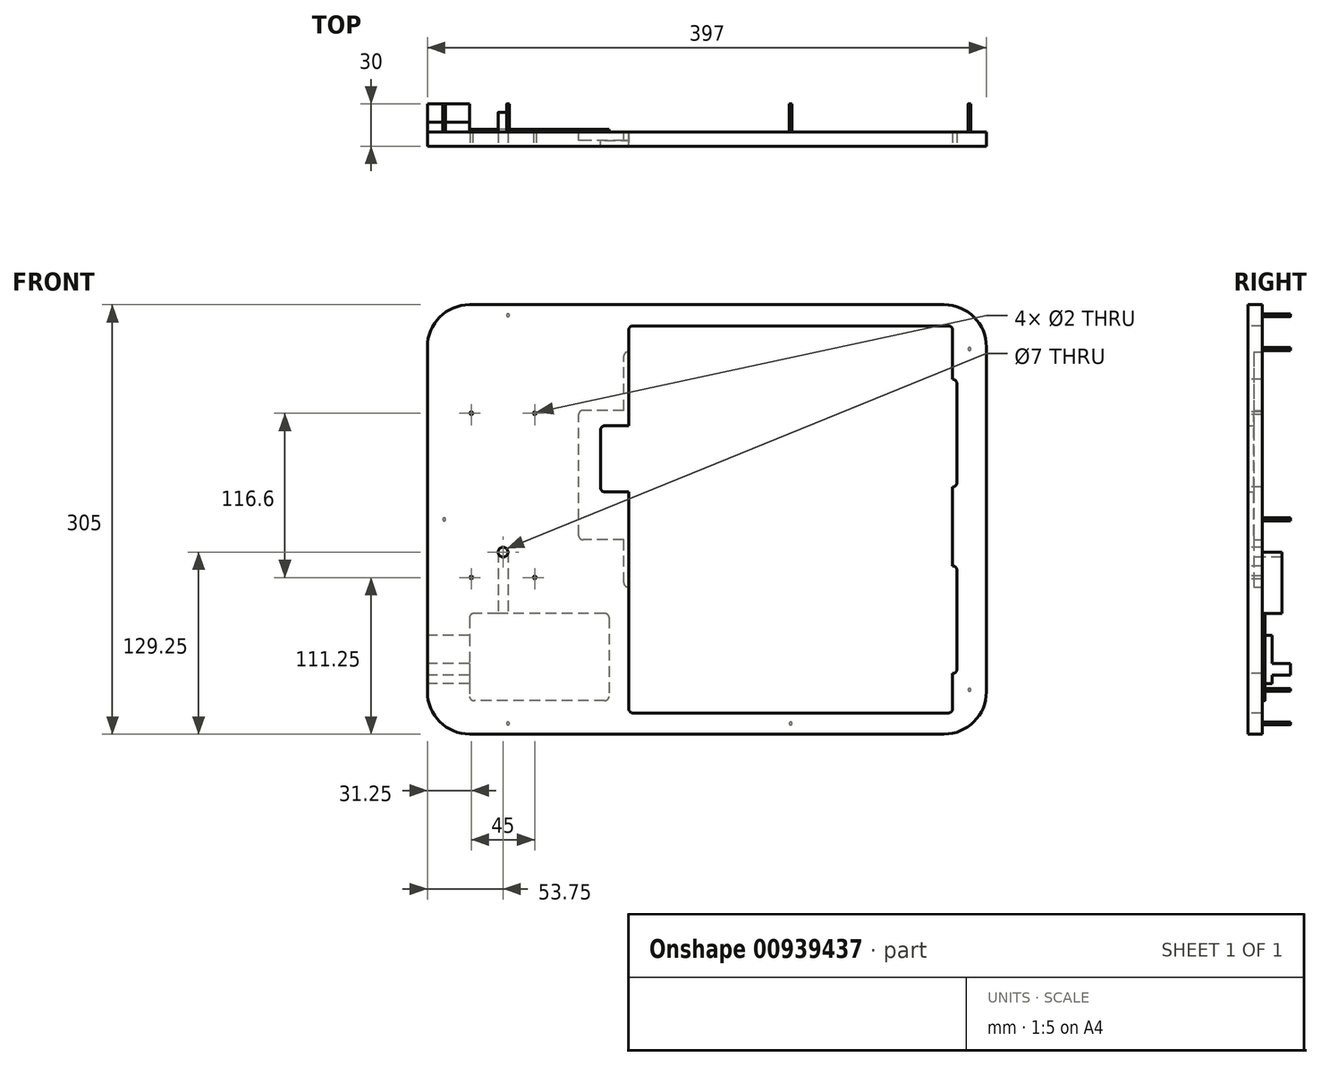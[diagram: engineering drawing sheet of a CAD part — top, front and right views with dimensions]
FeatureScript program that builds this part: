
annotation { "Feature Type Name" : "Feature", "Feature Type Description" : "" }
export const myFeature = defineFeature(function(context is Context, id is Id, definition is map)
    precondition{}
    {
        {
            var Q0;
            Q0=qCreatedBy(makeId("Front.planeOp"),FACE);
            var sketch = newSketch(context, id + "F0", { "sketchPlane" : qUnion([Q0])});
            skLineSegment(sketch, "E0.bottom", {"start": v(-198.5, 157.5) * mm, "end": v(198.5, 157.5) * mm});
            skLineSegment(sketch, "E0.top", {"start": v(-198.5, -147.5) * mm, "end": v(198.5, -147.5) * mm});
            skLineSegment(sketch, "E0.left", {"start": v(-198.5, 157.5) * mm, "end": v(-198.5, -147.5) * mm});
            skLineSegment(sketch, "E0.right", {"start": v(198.5, 157.5) * mm, "end": v(198.5, -147.5) * mm});
            skSolve(sketch);
        }
        {
            var Q0;
            Q0=makeQuery(id+"F0.imprint","IMPRINT",FACE,{"disambiguationData":[TD([[makeQuery(id+"F0.imprint","IMPRINT",EDGE,{"derivedFrom":sQuery(id+"F0.wireOp",EDGE,"E0.bottom")}),-1.0]])]});
            extrude(context, id + "F1", {"entities" : qUnion([Q0]), "depth" : 30 * mm, "offsetDistance" : 25 * mm});
        }
        {
            var Q0;
            Q0=makeQuery(id+"F1.opExtrude","CAP_FACE",FACE,{"disambiguationData":[OSD([sQuery(id+"F0.wireOp",EDGE,"E0.bottom"),sQuery(id+"F0.wireOp",EDGE,"E0.top"),sQuery(id+"F0.wireOp",EDGE,"E0.left"),sQuery(id+"F0.wireOp",EDGE,"E0.right")])],"isStart":false});
            var sketch = newSketch(context, id + "F2", { "sketchPlane" : qUnion([Q0])});
            skLineSegment(sketch, "E1.bottom", {"start": v(-55.5, 142.5) * mm, "end": v(174.5, 142.5) * mm});
            skLineSegment(sketch, "E1.top", {"start": v(-55.5, -132.5) * mm, "end": v(174.5, -132.5) * mm});
            skLineSegment(sketch, "E1.left", {"start": v(-55.5, 142.5) * mm, "end": v(-55.5, -132.5) * mm});
            skLineSegment(sketch, "E1.right", {"start": v(174.5, 142.5) * mm, "end": v(174.5, -132.5) * mm});
            skSolve(sketch);
        }
        {
            var Q0;
            Q0 = qSketchRegion(id + "F2", true);
            extrude(context, id + "F3", {"entities" : qUnion([Q0]), "operationType" : NewBodyOperationType.REMOVE, "endBound" : BoundingType.UP_TO_NEXT, "oppositeDirection" : true, "depth" : 25 * mm, "offsetDistance" : 25 * mm});
        }
        {
            var Q0;
            Q0=makeQuery(id+"F3.boolean.opBoolean","COPY",EDGE,{"derivedFrom":makeQuery(id+"F3.opExtrude","SWEPT_EDGE",EDGE,{"disambiguationData":[OSD([sQuery(id+"F2.wireOp",EDGE,"E1.bottom"),sQuery(id+"F2.wireOp",EDGE,"E1.left")])]})});
            var Q1;
            Q1=makeQuery(id+"F3.boolean.opBoolean","COPY",EDGE,{"derivedFrom":makeQuery(id+"F3.opExtrude","SWEPT_EDGE",EDGE,{"disambiguationData":[OSD([sQuery(id+"F2.wireOp",EDGE,"E1.bottom"),sQuery(id+"F2.wireOp",EDGE,"E1.right")])]})});
            var Q2;
            Q2=makeQuery(id+"F3.boolean.opBoolean","COPY",EDGE,{"derivedFrom":makeQuery(id+"F3.opExtrude","SWEPT_EDGE",EDGE,{"disambiguationData":[OSD([sQuery(id+"F2.wireOp",EDGE,"E1.top"),sQuery(id+"F2.wireOp",EDGE,"E1.right")])]})});
            var Q3;
            Q3=makeQuery(id+"F3.boolean.opBoolean","COPY",EDGE,{"derivedFrom":makeQuery(id+"F3.opExtrude","SWEPT_EDGE",EDGE,{"disambiguationData":[OSD([sQuery(id+"F2.wireOp",EDGE,"E1.top"),sQuery(id+"F2.wireOp",EDGE,"E1.left")])]})});
            fillet(context, id + "F4", {"entities" : qUnion([Q0, Q1, Q2, Q3]), "radius" : 3 * mm, "tangentPropagation" : true, "allowEdgeOverflow" : false});
        }
        {
            var Q0;
            Q0=makeQuery(id+"F1.opExtrude","SWEPT_EDGE",EDGE,{"disambiguationData":[OSD([sQuery(id+"F0.wireOp",EDGE,"E0.top"),sQuery(id+"F0.wireOp",EDGE,"E0.left")])]});
            var Q1;
            Q1=makeQuery(id+"F1.opExtrude","SWEPT_EDGE",EDGE,{"disambiguationData":[OSD([sQuery(id+"F0.wireOp",EDGE,"E0.bottom"),sQuery(id+"F0.wireOp",EDGE,"E0.left")])]});
            var Q2;
            Q2=makeQuery(id+"F1.opExtrude","SWEPT_EDGE",EDGE,{"disambiguationData":[OSD([sQuery(id+"F0.wireOp",EDGE,"E0.bottom"),sQuery(id+"F0.wireOp",EDGE,"E0.right")])]});
            var Q3;
            Q3=makeQuery(id+"F1.opExtrude","SWEPT_EDGE",EDGE,{"disambiguationData":[OSD([sQuery(id+"F0.wireOp",EDGE,"E0.top"),sQuery(id+"F0.wireOp",EDGE,"E0.right")])]});
            fillet(context, id + "F5", {"entities" : qUnion([Q0, Q1, Q2, Q3]), "radius" : 30 * mm, "tangentPropagation" : true, "allowEdgeOverflow" : false});
        }
        {
            var Q0;
            Q0=makeQuery(id+"F3.boolean.opBoolean","COPY",FACE,{"derivedFrom":makeQuery(id+"F3.opExtrude","SWEPT_FACE",FACE,{"disambiguationData":[OSD([sQuery(id+"F2.wireOp",EDGE,"E1.left")])]})});
            var sketch = newSketch(context, id + "F6", { "sketchPlane" : qUnion([Q0])});
            skLineSegment(sketch, "E2.bottom", {"start": v(-26, 124) * mm, "end": v(0, 124) * mm});
            skLineSegment(sketch, "E2.top", {"start": v(-26, -43) * mm, "end": v(0, -43) * mm});
            skLineSegment(sketch, "E2.left", {"start": v(-26, 124) * mm, "end": v(-26, -43) * mm});
            skLineSegment(sketch, "E2.right", {"start": v(0, 124) * mm, "end": v(0, -43) * mm});
            skSolve(sketch);
        }
        {
            var Q0;
            Q0=makeQuery(id+"F6.imprint","IMPRINT",FACE,{"disambiguationData":[TD([[makeQuery(id+"F6.imprint","IMPRINT",EDGE,{"derivedFrom":sQuery(id+"F6.wireOp",EDGE,"E2.bottom")}),-1.0]])]});
            extrude(context, id + "F7", {"entities" : qUnion([Q0]), "operationType" : NewBodyOperationType.REMOVE, "oppositeDirection" : true, "depth" : 3.5 * mm, "offsetDistance" : 25 * mm});
        }
        {
            var Q0;
            Q0=makeQuery(id+"F7.boolean.opBoolean","COPY",EDGE,{"derivedFrom":makeQuery(id+"F7.opExtrude","CAP_EDGE",EDGE,{"disambiguationData":[OSD([sQuery(id+"F6.wireOp",EDGE,"E2.top")])],"isStart":false})});
            var Q1;
            Q1=makeQuery(id+"F7.boolean.opBoolean","COPY",EDGE,{"derivedFrom":makeQuery(id+"F7.opExtrude","CAP_EDGE",EDGE,{"disambiguationData":[OSD([sQuery(id+"F6.wireOp",EDGE,"E2.bottom")])],"isStart":false})});
            fillet(context, id + "F8", {"entities" : qUnion([Q0, Q1]), "radius" : 3 * mm, "tangentPropagation" : true, "allowEdgeOverflow" : false});
        }
        {
            var Q0;
            Q0=makeQuery(id+"F7.boolean.opBoolean","COPY",FACE,{"derivedFrom":makeQuery(id+"F7.opExtrude","CAP_FACE",FACE,{"disambiguationData":[OSD([sQuery(id+"F6.wireOp",EDGE,"E2.bottom"),sQuery(id+"F6.wireOp",EDGE,"E2.top"),sQuery(id+"F6.wireOp",EDGE,"E2.left"),sQuery(id+"F6.wireOp",EDGE,"E2.right")])],"isStart":false})});
            var sketch = newSketch(context, id + "F9", { "sketchPlane" : qUnion([Q0])});
            skLineSegment(sketch, "E3.bottom", {"start": v(-23.6, 82.5) * mm, "end": v(0, 82.5) * mm});
            skLineSegment(sketch, "E3.top", {"start": v(-23.6, -9.5) * mm, "end": v(0, -9.5) * mm});
            skLineSegment(sketch, "E3.left", {"start": v(-23.6, 82.5) * mm, "end": v(-23.6, -9.5) * mm});
            skLineSegment(sketch, "E3.right", {"start": v(0, 82.5) * mm, "end": v(0, -9.5) * mm});
            skSolve(sketch);
        }
        {
            var Q0;
            Q0=makeQuery(id+"F1.opExtrude","CAP_FACE",FACE,{"disambiguationData":[OSD([sQuery(id+"F0.wireOp",EDGE,"E0.bottom"),sQuery(id+"F0.wireOp",EDGE,"E0.top"),sQuery(id+"F0.wireOp",EDGE,"E0.left"),sQuery(id+"F0.wireOp",EDGE,"E0.right")])],"isStart":true});
            var sketch = newSketch(context, id + "F10", { "sketchPlane" : qUnion([Q0])});
            skLineSegment(sketch, "E4.bottom", {"start": v(59, -9.5) * mm, "end": v(91, -9.5) * mm});
            skLineSegment(sketch, "E4.top", {"start": v(59, 82.5) * mm, "end": v(91, 82.5) * mm});
            skLineSegment(sketch, "E4.left", {"start": v(59, -9.5) * mm, "end": v(59, 82.5) * mm});
            skLineSegment(sketch, "E4.right", {"start": v(91, -9.5) * mm, "end": v(91, 82.5) * mm});
            skSolve(sketch);
        }
        {
            var Q0;
            Q0 = qSketchRegion(id + "F10", true);
            extrude(context, id + "F11", {"entities" : qUnion([Q0]), "operationType" : NewBodyOperationType.REMOVE, "oppositeDirection" : true, "depth" : 26 * mm, "offsetDistance" : 25 * mm});
        }
        {
            var Q0;
            Q0=makeQuery(id+"F11.boolean.opBoolean","COPY",EDGE,{"derivedFrom":makeQuery(id+"F11.opExtrude","SWEPT_EDGE",EDGE,{"disambiguationData":[OSD([sQuery(id+"F10.wireOp",EDGE,"E4.bottom"),sQuery(id+"F10.wireOp",EDGE,"E4.right")])]})});
            var Q1;
            Q1=makeQuery(id+"F11.boolean.opBoolean","COPY",EDGE,{"derivedFrom":makeQuery(id+"F11.opExtrude","SWEPT_EDGE",EDGE,{"disambiguationData":[OSD([sQuery(id+"F10.wireOp",EDGE,"E4.top"),sQuery(id+"F10.wireOp",EDGE,"E4.right")])]})});
            fillet(context, id + "F12", {"entities" : qUnion([Q0, Q1]), "radius" : 3 * mm, "tangentPropagation" : true, "allowEdgeOverflow" : false});
        }
        {
            var Q0;
            Q0=makeQuery(id+"F3.boolean.opBoolean","COPY",FACE,{"derivedFrom":makeQuery(id+"F3.opExtrude","SWEPT_FACE",FACE,{"disambiguationData":[OSD([sQuery(id+"F2.wireOp",EDGE,"E1.left")])]})});
            var sketch = newSketch(context, id + "F13", { "sketchPlane" : qUnion([Q0])});
            skLineSegment(sketch, "E5.bottom", {"start": v(-30, 71.5) * mm, "end": v(-26, 71.5) * mm});
            skLineSegment(sketch, "E5.top", {"start": v(-30, 24.5) * mm, "end": v(-26, 24.5) * mm});
            skLineSegment(sketch, "E5.left", {"start": v(-30, 71.5) * mm, "end": v(-30, 24.5) * mm});
            skLineSegment(sketch, "E5.right", {"start": v(-26, 71.5) * mm, "end": v(-26, 24.5) * mm});
            skSolve(sketch);
        }
        {
            var Q0;
            Q0 = qSketchRegion(id + "F13", true);
            extrude(context, id + "F14", {"entities" : qUnion([Q0]), "operationType" : NewBodyOperationType.REMOVE, "oppositeDirection" : true, "depth" : 20 * mm, "offsetDistance" : 25 * mm});
        }
        {
            var Q0;
            Q0=makeQuery(id+"F14.boolean.opBoolean","COPY",EDGE,{"derivedFrom":makeQuery(id+"F14.opExtrude","CAP_EDGE",EDGE,{"disambiguationData":[OSD([sQuery(id+"F13.wireOp",EDGE,"E5.top")])],"isStart":false})});
            var Q1;
            Q1=makeQuery(id+"F14.boolean.opBoolean","COPY",EDGE,{"derivedFrom":makeQuery(id+"F14.opExtrude","CAP_EDGE",EDGE,{"disambiguationData":[OSD([sQuery(id+"F13.wireOp",EDGE,"E5.bottom")])],"isStart":false})});
            fillet(context, id + "F15", {"entities" : qUnion([Q0, Q1]), "radius" : 3 * mm, "tangentPropagation" : true, "allowEdgeOverflow" : false});
        }
        {
            var Q0;
            Q0=makeQuery(id+"F3.boolean.opBoolean","COPY",FACE,{"derivedFrom":makeQuery(id+"F3.opExtrude","SWEPT_FACE",FACE,{"disambiguationData":[OSD([sQuery(id+"F2.wireOp",EDGE,"E1.right")])]})});
            var sketch = newSketch(context, id + "F16", { "sketchPlane" : qUnion([Q0])});
            skLineSegment(sketch, "E6.bottom", {"start": v(0, -28) * mm, "end": v(30, -28) * mm});
            skLineSegment(sketch, "E6.top", {"start": v(0, -104.5) * mm, "end": v(30, -104.5) * mm});
            skLineSegment(sketch, "E6.left", {"start": v(0, -28) * mm, "end": v(0, -104.5) * mm});
            skLineSegment(sketch, "E6.right", {"start": v(30, -28) * mm, "end": v(30, -104.5) * mm});
            skLineSegment(sketch, "E7.bottom", {"start": v(0, 104.5) * mm, "end": v(30, 104.5) * mm});
            skLineSegment(sketch, "E7.top", {"start": v(0, 28) * mm, "end": v(30, 28) * mm});
            skLineSegment(sketch, "E7.left", {"start": v(0, 104.5) * mm, "end": v(0, 28) * mm});
            skLineSegment(sketch, "E7.right", {"start": v(30, 104.5) * mm, "end": v(30, 28) * mm});
            skSolve(sketch);
        }
        {
            var Q0;
            Q0 = qSketchRegion(id + "F16", true);
            extrude(context, id + "F17", {"entities" : qUnion([Q0]), "operationType" : NewBodyOperationType.REMOVE, "oppositeDirection" : true, "depth" : 3 * mm, "offsetDistance" : 25 * mm});
        }
        {
            var Q0;
            Q0=makeQuery(id+"F17.boolean.opBoolean","COPY",EDGE,{"derivedFrom":makeQuery(id+"F17.opExtrude","CAP_EDGE",EDGE,{"disambiguationData":[OSD([sQuery(id+"F16.wireOp",EDGE,"E6.top")])],"isStart":false})});
            var Q1;
            Q1=makeQuery(id+"F17.boolean.opBoolean","COPY",EDGE,{"derivedFrom":makeQuery(id+"F17.opExtrude","CAP_EDGE",EDGE,{"disambiguationData":[OSD([sQuery(id+"F16.wireOp",EDGE,"E7.top")])],"isStart":false})});
            var Q2;
            Q2=makeQuery(id+"F17.boolean.opBoolean","COPY",EDGE,{"derivedFrom":makeQuery(id+"F17.opExtrude","CAP_EDGE",EDGE,{"disambiguationData":[OSD([sQuery(id+"F16.wireOp",EDGE,"E7.bottom")])],"isStart":false})});
            var Q3;
            Q3=makeQuery(id+"F17.boolean.opBoolean","COPY",EDGE,{"derivedFrom":makeQuery(id+"F17.opExtrude","CAP_EDGE",EDGE,{"disambiguationData":[OSD([sQuery(id+"F16.wireOp",EDGE,"E6.bottom")])],"isStart":false})});
            fillet(context, id + "F18", {"entities" : qUnion([Q0, Q1, Q2, Q3]), "radius" : 3 * mm, "tangentPropagation" : true, "allowEdgeOverflow" : false});
        }
        {
            var Q0;
            Q0=makeQuery(id+"F1.opExtrude","CAP_FACE",FACE,{"disambiguationData":[OSD([sQuery(id+"F0.wireOp",EDGE,"E0.bottom"),sQuery(id+"F0.wireOp",EDGE,"E0.top"),sQuery(id+"F0.wireOp",EDGE,"E0.left"),sQuery(id+"F0.wireOp",EDGE,"E0.right")])],"isStart":false});
            var sketch = newSketch(context, id + "F19", { "sketchPlane" : qUnion([Q0])});
            skCircle(sketch, "E8", {"center": v(-144.75, -18.25) * mm, "radius": 3.5 * mm});
            skSolve(sketch);
        }
        {
            var Q0;
            Q0 = qSketchRegion(id + "F19", true);
            extrude(context, id + "F20", {"entities" : qUnion([Q0]), "operationType" : NewBodyOperationType.REMOVE, "oppositeDirection" : true, "depth" : 30 * mm, "offsetDistance" : 25 * mm});
        }
        {
            var Q0;
            Q0=makeQuery(id+"F1.opExtrude","CAP_FACE",FACE,{"disambiguationData":[OSD([sQuery(id+"F0.wireOp",EDGE,"E0.bottom"),sQuery(id+"F0.wireOp",EDGE,"E0.top"),sQuery(id+"F0.wireOp",EDGE,"E0.left"),sQuery(id+"F0.wireOp",EDGE,"E0.right")])],"isStart":true});
            var sketch = newSketch(context, id + "F21", { "sketchPlane" : qUnion([Q0])});
            skLineSegment(sketch, "E9.bottom", {"start": v(69.5, -61.75) * mm, "end": v(168.5, -61.75) * mm});
            skLineSegment(sketch, "E9.top", {"start": v(69.5, -123.75) * mm, "end": v(168.5, -123.75) * mm});
            skLineSegment(sketch, "E9.left", {"start": v(69.5, -61.75) * mm, "end": v(69.5, -123.75) * mm});
            skLineSegment(sketch, "E9.right", {"start": v(168.5, -61.75) * mm, "end": v(168.5, -123.75) * mm});
            skSolve(sketch);
        }
        {
            var Q0;
            Q0 = qSketchRegion(id + "F21", true);
            var Q1;
            Q1 = qSketchRegion(id + "F24", true);
            extrude(context, id + "F22", {"entities" : qUnion([Q0, Q1]), "operationType" : NewBodyOperationType.REMOVE, "oppositeDirection" : true, "depth" : 18 * mm, "offsetDistance" : 25 * mm});
        }
        {
            var Q0;
            Q0=makeQuery(id+"F22.boolean.opBoolean","COPY",EDGE,{"derivedFrom":makeQuery(id+"F22.opExtrude","SWEPT_EDGE",EDGE,{"disambiguationData":[OSD([sQuery(id+"F21.wireOp",EDGE,"E9.top"),sQuery(id+"F21.wireOp",EDGE,"E9.right")])]})});
            var Q1;
            Q1=makeQuery(id+"F22.boolean.opBoolean","COPY",EDGE,{"derivedFrom":makeQuery(id+"F22.opExtrude","SWEPT_EDGE",EDGE,{"disambiguationData":[OSD([sQuery(id+"F21.wireOp",EDGE,"E9.top"),sQuery(id+"F21.wireOp",EDGE,"E9.left")])]})});
            var Q2;
            Q2=makeQuery(id+"F22.boolean.opBoolean","COPY",EDGE,{"derivedFrom":makeQuery(id+"F22.opExtrude","SWEPT_EDGE",EDGE,{"disambiguationData":[OSD([sQuery(id+"F21.wireOp",EDGE,"E9.bottom"),sQuery(id+"F21.wireOp",EDGE,"E9.left")])]})});
            var Q3;
            Q3=makeQuery(id+"F22.boolean.opBoolean","COPY",EDGE,{"derivedFrom":makeQuery(id+"F22.opExtrude","SWEPT_EDGE",EDGE,{"disambiguationData":[OSD([sQuery(id+"F21.wireOp",EDGE,"E9.bottom"),sQuery(id+"F21.wireOp",EDGE,"E9.right")])]})});
            fillet(context, id + "F23", {"entities" : qUnion([Q0, Q1, Q2, Q3]), "radius" : 3 * mm, "tangentPropagation" : true, "allowEdgeOverflow" : false});
        }
        {
            var Q0;
            Q0=makeQuery(id+"F1.opExtrude","CAP_FACE",FACE,{"disambiguationData":[OSD([sQuery(id+"F0.wireOp",EDGE,"E0.bottom"),sQuery(id+"F0.wireOp",EDGE,"E0.top"),sQuery(id+"F0.wireOp",EDGE,"E0.left"),sQuery(id+"F0.wireOp",EDGE,"E0.right")])],"isStart":true});
            var sketch = newSketch(context, id + "F24", { "sketchPlane" : qUnion([Q0])});
            skLineSegment(sketch, "E10", {"start": v(141.25, -18.25) * mm, "end": v(141.25, -61.75) * mm});
            skLineSegment(sketch, "E11", {"start": v(148.25, -18.25) * mm, "end": v(148.25, -61.75) * mm});
            skSolve(sketch);
        }
        {
            var Q0;
            {var subQ0=sQuery(id+"F24.wireOp",EDGE,"E10");Q0=makeQuery(id+"F24.imprint","IMPRINT",FACE,{"disambiguationData":[TD([[makeQuery(id+"F24.imprint","IMPRINT",EDGE,{"derivedFrom":subQ0}),1.0]])]});}
            extrude(context, id + "F25", {"entities" : qUnion([Q0]), "operationType" : NewBodyOperationType.REMOVE, "oppositeDirection" : true, "depth" : 6 * mm, "offsetDistance" : 25 * mm});
        }
        {
            var Q0;
            Q0=makeQuery(id+"F1.opExtrude","SWEPT_FACE",FACE,{"disambiguationData":[OSD([sQuery(id+"F0.wireOp",EDGE,"E0.left")])]});
            var sketch = newSketch(context, id + "F26", { "sketchPlane" : qUnion([Q0])});
            skLineSegment(sketch, "E12.bottom", {"start": v(0, -77.5) * mm, "end": v(13, -77.5) * mm});
            skLineSegment(sketch, "E12.top", {"start": v(0, -97.5) * mm, "end": v(13, -97.5) * mm});
            skLineSegment(sketch, "E12.left", {"start": v(0, -77.5) * mm, "end": v(0, -97.5) * mm});
            skLineSegment(sketch, "E12.right", {"start": v(13, -77.5) * mm, "end": v(13, -97.5) * mm});
            skLineSegment(sketch, "E13.bottom", {"start": v(0, -105.5) * mm, "end": v(13, -105.5) * mm});
            skLineSegment(sketch, "E13.top", {"start": v(0, -111.5) * mm, "end": v(13, -111.5) * mm});
            skLineSegment(sketch, "E13.left", {"start": v(0, -105.5) * mm, "end": v(0, -111.5) * mm});
            skLineSegment(sketch, "E13.right", {"start": v(13, -105.5) * mm, "end": v(13, -111.5) * mm});
            skSolve(sketch);
        }
        {
            var Q0;
            Q0 = qSketchRegion(id + "F26", true);
            extrude(context, id + "F27", {"entities" : qUnion([Q0]), "operationType" : NewBodyOperationType.REMOVE, "oppositeDirection" : true, "depth" : 30 * mm, "offsetDistance" : 25 * mm});
        }
        {
            var Q0;
            Q0=makeQuery(id+"F1.opExtrude","CAP_FACE",FACE,{"disambiguationData":[OSD([sQuery(id+"F0.wireOp",EDGE,"E0.bottom"),sQuery(id+"F0.wireOp",EDGE,"E0.top"),sQuery(id+"F0.wireOp",EDGE,"E0.left"),sQuery(id+"F0.wireOp",EDGE,"E0.right")])],"isStart":false});
            var sketch = newSketch(context, id + "F28", { "sketchPlane" : qUnion([Q0])});
            skCircle(sketch, "E14", {"center": v(-167.25, 80.35) * mm, "radius": 1 * mm});
            skCircle(sketch, "E15", {"center": v(-167.25, -36.25) * mm, "radius": 1 * mm});
            skCircle(sketch, "E16", {"center": v(-122.25, -36.25) * mm, "radius": 1 * mm});
            skCircle(sketch, "E17", {"center": v(-122.25, 80.35) * mm, "radius": 1 * mm});
            skLineSegment(sketch, "E18", {"start": v(-144.75, 61.68) * mm, "end": v(-144.75, -18.85) * mm});
            skLineSegment(sketch, "E19", {"start": v(-179, 96.95) * mm, "end": v(-109.8, 96.95) * mm});
            skSolve(sketch);
        }
        {
            var Q0;
            Q0 = qSketchRegion(id + "F28", true);
            extrude(context, id + "F29", {"entities" : qUnion([Q0]), "operationType" : NewBodyOperationType.REMOVE, "oppositeDirection" : true, "depth" : 30 * mm, "offsetDistance" : 25 * mm});
        }
        {
            var Q0;
            {var subQ1=sQuery(id+"F0.wireOp",EDGE,"E0.right");var subQ2=sQuery(id+"F0.wireOp",EDGE,"E0.top");var subQ5=sQuery(id+"F0.wireOp",EDGE,"E0.left");var subQ8=sQuery(id+"F0.wireOp",EDGE,"E0.bottom");Q0=makeQuery(id+"F27.boolean.opBoolean","SPLIT",FACE,{"disambiguationData":[TD([makeQuery(id+"F1.opExtrude","SWEPT_FACE",FACE,{"disambiguationData":[OSD([subQ8])]})])],"derivedFrom":makeQuery(id+"F1.opExtrude","CAP_FACE",FACE,{"disambiguationData":[OSD([subQ8,subQ2,subQ5,subQ1])],"isStart":true})});}
            var sketch = newSketch(context, id + "F30", { "sketchPlane" : qUnion([Q0])});
            skLineSegment(sketch, "E20.bottom", {"start": v(186.5, 150) * mm, "end": v(-186.5, 150) * mm});
            skLineSegment(sketch, "E20.top", {"start": v(186.5, -140) * mm, "end": v(-186.5, -140) * mm});
            skLineSegment(sketch, "E20.left", {"start": v(186.5, 150) * mm, "end": v(186.5, -140) * mm});
            skLineSegment(sketch, "E20.right", {"start": v(-186.5, 150) * mm, "end": v(-186.5, -140) * mm});
            skCircle(sketch, "E21", {"center": v(-186.5, 126) * mm, "radius": 1 * mm});
            skCircle(sketch, "E22", {"center": v(-186.5, 5) * mm, "radius": 1 * mm});
            skCircle(sketch, "E23", {"center": v(-186.5, -116) * mm, "radius": 1 * mm});
            skCircle(sketch, "E24", {"center": v(-59.5, 150) * mm, "radius": 1 * mm});
            skPoint(sketch, "E24.centerSnap0", {"position": v(-59.5, 142.5) * mm});
            skCircle(sketch, "E25", {"center": v(-59.5, -140) * mm, "radius": 1 * mm});
            skCircle(sketch, "E26", {"center": v(141.25, -140) * mm, "radius": 1 * mm});
            skCircle(sketch, "E27", {"center": v(141.25, 150) * mm, "radius": 1 * mm});
            skCircle(sketch, "E28", {"center": v(186.5, 5) * mm, "radius": 1 * mm});
            skSolve(sketch);
        }
        {
            var Q0;
            {var subQ0=sQuery(id+"F30.wireOp",EDGE,"E21");var subQ1=sQuery(id+"F30.wireOp",EDGE,"E20.right");var subQ2=makeQuery(id+"F30.imprint","INTERSECT",VERTEX,{"disambiguationData":[OD(0.0)],"derivedFrom":[subQ1,subQ0]});Q0=makeQuery(id+"F30.imprint","IMPRINT",FACE,{"disambiguationData":[TD([[makeQuery(id+"F30.imprint","IMPRINT",EDGE,{"disambiguationData":[TD([[subQ2,-1.0]])],"derivedFrom":subQ1}),-1.0]])]});}
            var Q1;
            {var subQ0=sQuery(id+"F30.wireOp",EDGE,"E21");var subQ1=sQuery(id+"F30.wireOp",EDGE,"E20.right");var subQ2=makeQuery(id+"F30.imprint","INTERSECT",VERTEX,{"disambiguationData":[OD(0.0)],"derivedFrom":[subQ1,subQ0]});Q1=makeQuery(id+"F30.imprint","IMPRINT",FACE,{"disambiguationData":[TD([[makeQuery(id+"F30.imprint","IMPRINT",EDGE,{"disambiguationData":[TD([[subQ2,-1.0]])],"derivedFrom":subQ1}),1.0]])]});}
            var Q2;
            {var subQ0=sQuery(id+"F30.wireOp",EDGE,"E24");var subQ1=sQuery(id+"F30.wireOp",EDGE,"E20.bottom");var subQ2=makeQuery(id+"F30.imprint","INTERSECT",VERTEX,{"disambiguationData":[OD(0.0)],"derivedFrom":[subQ1,subQ0]});Q2=makeQuery(id+"F30.imprint","IMPRINT",FACE,{"disambiguationData":[TD([[makeQuery(id+"F30.imprint","IMPRINT",EDGE,{"disambiguationData":[TD([[subQ2,-1.0]])],"derivedFrom":subQ1}),1.0]])]});}
            var Q3;
            {var subQ0=sQuery(id+"F30.wireOp",EDGE,"E24");var subQ1=sQuery(id+"F30.wireOp",EDGE,"E20.bottom");var subQ2=makeQuery(id+"F30.imprint","INTERSECT",VERTEX,{"disambiguationData":[OD(0.0)],"derivedFrom":[subQ1,subQ0]});Q3=makeQuery(id+"F30.imprint","IMPRINT",FACE,{"disambiguationData":[TD([[makeQuery(id+"F30.imprint","IMPRINT",EDGE,{"disambiguationData":[TD([[subQ2,-1.0]])],"derivedFrom":subQ1}),-1.0]])]});}
            var Q4;
            {var subQ0=sQuery(id+"F30.wireOp",EDGE,"E27");var subQ1=sQuery(id+"F30.wireOp",EDGE,"E20.bottom");var subQ2=makeQuery(id+"F30.imprint","INTERSECT",VERTEX,{"disambiguationData":[OD(0.0)],"derivedFrom":[subQ1,subQ0]});Q4=makeQuery(id+"F30.imprint","IMPRINT",FACE,{"disambiguationData":[TD([[makeQuery(id+"F30.imprint","IMPRINT",EDGE,{"disambiguationData":[TD([[subQ2,-1.0]])],"derivedFrom":subQ1}),-1.0]])]});}
            var Q5;
            {var subQ0=sQuery(id+"F30.wireOp",EDGE,"E27");var subQ1=sQuery(id+"F30.wireOp",EDGE,"E20.bottom");var subQ2=makeQuery(id+"F30.imprint","INTERSECT",VERTEX,{"disambiguationData":[OD(0.0)],"derivedFrom":[subQ1,subQ0]});Q5=makeQuery(id+"F30.imprint","IMPRINT",FACE,{"disambiguationData":[TD([[makeQuery(id+"F30.imprint","IMPRINT",EDGE,{"disambiguationData":[TD([[subQ2,-1.0]])],"derivedFrom":subQ1}),1.0]])]});}
            var Q6;
            {var subQ0=sQuery(id+"F30.wireOp",EDGE,"E28");var subQ1=sQuery(id+"F30.wireOp",EDGE,"E20.left");var subQ2=makeQuery(id+"F30.imprint","INTERSECT",VERTEX,{"disambiguationData":[OD(0.0)],"derivedFrom":[subQ1,subQ0]});Q6=makeQuery(id+"F30.imprint","IMPRINT",FACE,{"disambiguationData":[TD([[makeQuery(id+"F30.imprint","IMPRINT",EDGE,{"disambiguationData":[TD([[subQ2,-1.0]])],"derivedFrom":subQ1}),1.0]])]});}
            var Q7;
            {var subQ0=sQuery(id+"F30.wireOp",EDGE,"E28");var subQ1=sQuery(id+"F30.wireOp",EDGE,"E20.left");var subQ2=makeQuery(id+"F30.imprint","INTERSECT",VERTEX,{"disambiguationData":[OD(0.0)],"derivedFrom":[subQ1,subQ0]});Q7=makeQuery(id+"F30.imprint","IMPRINT",FACE,{"disambiguationData":[TD([[makeQuery(id+"F30.imprint","IMPRINT",EDGE,{"disambiguationData":[TD([[subQ2,-1.0]])],"derivedFrom":subQ1}),-1.0]])]});}
            var Q8;
            {var subQ0=sQuery(id+"F30.wireOp",EDGE,"E26");var subQ1=sQuery(id+"F30.wireOp",EDGE,"E20.top");var subQ2=makeQuery(id+"F30.imprint","INTERSECT",VERTEX,{"disambiguationData":[OD(0.0)],"derivedFrom":[subQ1,subQ0]});Q8=makeQuery(id+"F30.imprint","IMPRINT",FACE,{"disambiguationData":[TD([[makeQuery(id+"F30.imprint","IMPRINT",EDGE,{"disambiguationData":[TD([[subQ2,-1.0]])],"derivedFrom":subQ1}),-1.0]])]});}
            var Q9;
            {var subQ0=sQuery(id+"F30.wireOp",EDGE,"E26");var subQ1=sQuery(id+"F30.wireOp",EDGE,"E20.top");var subQ2=makeQuery(id+"F30.imprint","INTERSECT",VERTEX,{"disambiguationData":[OD(0.0)],"derivedFrom":[subQ1,subQ0]});Q9=makeQuery(id+"F30.imprint","IMPRINT",FACE,{"disambiguationData":[TD([[makeQuery(id+"F30.imprint","IMPRINT",EDGE,{"disambiguationData":[TD([[subQ2,-1.0]])],"derivedFrom":subQ1}),1.0]])]});}
            var Q10;
            {var subQ0=sQuery(id+"F30.wireOp",EDGE,"E25");var subQ1=sQuery(id+"F30.wireOp",EDGE,"E20.top");var subQ2=makeQuery(id+"F30.imprint","INTERSECT",VERTEX,{"disambiguationData":[OD(0.0)],"derivedFrom":[subQ1,subQ0]});Q10=makeQuery(id+"F30.imprint","IMPRINT",FACE,{"disambiguationData":[TD([[makeQuery(id+"F30.imprint","IMPRINT",EDGE,{"disambiguationData":[TD([[subQ2,-1.0]])],"derivedFrom":subQ1}),-1.0]])]});}
            var Q11;
            {var subQ0=sQuery(id+"F30.wireOp",EDGE,"E25");var subQ1=sQuery(id+"F30.wireOp",EDGE,"E20.top");var subQ2=makeQuery(id+"F30.imprint","INTERSECT",VERTEX,{"disambiguationData":[OD(0.0)],"derivedFrom":[subQ1,subQ0]});Q11=makeQuery(id+"F30.imprint","IMPRINT",FACE,{"disambiguationData":[TD([[makeQuery(id+"F30.imprint","IMPRINT",EDGE,{"disambiguationData":[TD([[subQ2,-1.0]])],"derivedFrom":subQ1}),1.0]])]});}
            var Q12;
            {var subQ0=sQuery(id+"F30.wireOp",EDGE,"E23");var subQ1=sQuery(id+"F30.wireOp",EDGE,"E20.right");var subQ2=makeQuery(id+"F30.imprint","INTERSECT",VERTEX,{"disambiguationData":[OD(0.0)],"derivedFrom":[subQ1,subQ0]});Q12=makeQuery(id+"F30.imprint","IMPRINT",FACE,{"disambiguationData":[TD([[makeQuery(id+"F30.imprint","IMPRINT",EDGE,{"disambiguationData":[TD([[subQ2,-1.0]])],"derivedFrom":subQ1}),1.0]])]});}
            var Q13;
            {var subQ0=sQuery(id+"F30.wireOp",EDGE,"E23");var subQ1=sQuery(id+"F30.wireOp",EDGE,"E20.right");var subQ2=makeQuery(id+"F30.imprint","INTERSECT",VERTEX,{"disambiguationData":[OD(0.0)],"derivedFrom":[subQ1,subQ0]});Q13=makeQuery(id+"F30.imprint","IMPRINT",FACE,{"disambiguationData":[TD([[makeQuery(id+"F30.imprint","IMPRINT",EDGE,{"disambiguationData":[TD([[subQ2,-1.0]])],"derivedFrom":subQ1}),-1.0]])]});}
            var Q14;
            {var subQ0=sQuery(id+"F30.wireOp",EDGE,"E22");var subQ1=sQuery(id+"F30.wireOp",EDGE,"E20.right");var subQ2=makeQuery(id+"F30.imprint","INTERSECT",VERTEX,{"disambiguationData":[OD(0.0)],"derivedFrom":[subQ1,subQ0]});Q14=makeQuery(id+"F30.imprint","IMPRINT",FACE,{"disambiguationData":[TD([[makeQuery(id+"F30.imprint","IMPRINT",EDGE,{"disambiguationData":[TD([[subQ2,-1.0]])],"derivedFrom":subQ1}),-1.0]])]});}
            var Q15;
            {var subQ0=sQuery(id+"F30.wireOp",EDGE,"E22");var subQ1=sQuery(id+"F30.wireOp",EDGE,"E20.right");var subQ2=makeQuery(id+"F30.imprint","INTERSECT",VERTEX,{"disambiguationData":[OD(0.0)],"derivedFrom":[subQ1,subQ0]});Q15=makeQuery(id+"F30.imprint","IMPRINT",FACE,{"disambiguationData":[TD([[makeQuery(id+"F30.imprint","IMPRINT",EDGE,{"disambiguationData":[TD([[subQ2,-1.0]])],"derivedFrom":subQ1}),1.0]])]});}
            extrude(context, id + "F31", {"entities" : qUnion([Q0, Q1, Q2, Q3, Q4, Q5, Q6, Q7, Q8, Q9, Q10, Q11, Q12, Q13, Q14, Q15]), "operationType" : NewBodyOperationType.REMOVE, "oppositeDirection" : true, "depth" : 20 * mm, "offsetDistance" : 25 * mm});
        }
    });
